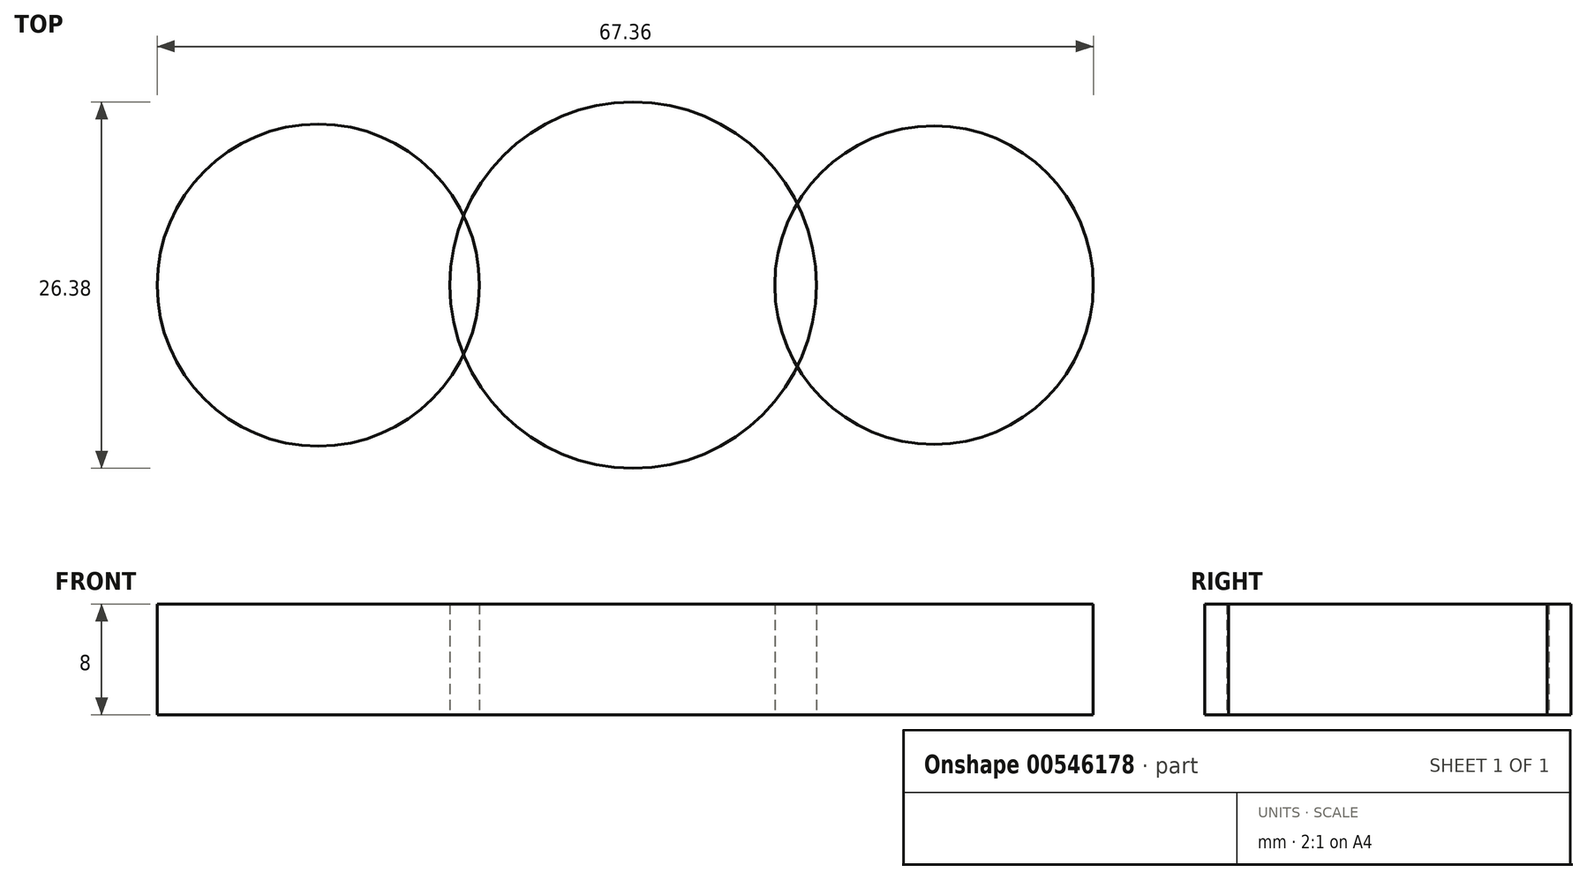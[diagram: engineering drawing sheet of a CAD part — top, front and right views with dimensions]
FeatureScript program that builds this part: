
annotation { "Feature Type Name" : "Feature", "Feature Type Description" : "" }
export const myFeature = defineFeature(function(context is Context, id is Id, definition is map)
    precondition{}
    {
        {
            var Q0;
            Q0=qCreatedBy(makeId("Top.planeOp"),FACE);
            var sketch = newSketch(context, id + "F0", { "sketchPlane" : qUnion([Q0])});
            skCircle(sketch, "E0", {"center": v(0, 0) * mm, "radius": 13.19 * mm});
            skSolve(sketch);
        }
        {
            var Q0;
            Q0=makeQuery(id+"F0.imprint","IMPRINT",FACE,{"disambiguationData":[TD([[makeQuery(id+"F0.imprint","IMPRINT",EDGE,{"derivedFrom":sQuery(id+"F0.wireOp",EDGE,"E0")}),1.0]])]});
            var sketch = newSketch(context, id + "F1", { "sketchPlane" : qUnion([Q0])});
            skCircle(sketch, "E1", {"center": v(-22.65, 0) * mm, "radius": 11.6 * mm});
            skCircle(sketch, "E2", {"center": v(21.66, 0) * mm, "radius": 11.46 * mm});
            skSolve(sketch);
        }
        {
            var Q0;
            Q0 = qSketchRegion(id + "F1", true);
            var Q1;
            Q1 = qSketchRegion(id + "F0", true);
            extrude(context, id + "F2", {"entities" : qUnion([Q0, Q1]), "depth" : 8 * mm, "offsetDistance" : 25 * mm});
        }
    });
